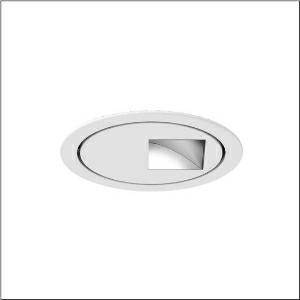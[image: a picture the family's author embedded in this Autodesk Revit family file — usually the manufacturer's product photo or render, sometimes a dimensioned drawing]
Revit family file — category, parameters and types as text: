
# Revit family: lunis_11_mini_round_51dk11b72wn21
name_source: partatom
category: Lighting Fixtures
units: mm (PartAtom-declared; Revit-internal decimal feet)

## family parameters
Cut with Voids When Loaded = No
Host = Face
Light Source = No
Part Type = Normal
Room Calculation Point = No
Round Connector Dimension = Use Diameter
Shared = No

## types (1)
- Lunis 11 mini round (1 x LED 4000K / CRI = 90 (unbekannt), 2120 lm, 4000K)
    Apparent Load = 28 VA
    CIE Flux Codes = 44 77 97 100 100
    Color Rendering = 90
    Color Temperature = 4000K
    Default Elevation = 1800 mm
    Description = Lunis 11 mini round, downlight, light control with wallwasher, of highly reflective aluminium, highly specular, light emission: direct distribution, LED rated luminous flux: 2.120lm, light colour: 940, control gear: ECG, with terminal, 3-pole, mains connection: 220..230V, AC/DC, 0/50..60Hz, LED module, luminaire module, of aluminium, highly specular, white, diameter: 176mm, clamping range: 1..40mm, recessing ring, of plastic, traffic white (RAL 9016), protection rating (complete): IP20, insulation class (complete): insulation class II (safety insulation), certification: CE, permissible ambient temperature for indoor applications: 0..+35°C, packaging unit: 1 piece
    Height = 0 mm  [stored 0 ft]
    Lamp = 1 x LED 4000K / CRI >= 90 (unbekannt)
    Lamp Light Flux = 2120 lm
    Lamp count = 1
    Length = 176 mm
    Luminous efficacy = 75 lm/W
    Manufacturer = Siteco
    ModVariant = No
    Model = 51DK11B72WN21
    Mounting Place = Ceiling
    Mounting Type = Recessed
    Number of Poles = 1
    OnlyDefault = Yes
    Power Factor = 1
    Product Name = Lunis 11 mini round
    Product group = downlight
    ProductGroupID = 400
    Protection Class = Protection class II
    Protection Degree = IP 20
    RLX_Detail_Level = 1
    RLX_Emergency_Light_Flux = 0 lm
    RLX_Emergency_Type = 0
    RLX_Emergency_Type_DB = No
    RlxData = <blob elided: 59265 chars, md5=d7e8e7a5>
    Socket = socket
    Standby Power = 0 W
    System Light Flux = 2120 lm
    System Power = 28 W
    Type Comments = Product without accessories
    Type Image = l_1004772.jpg
    URL = http://relux.com
    VarID = ---
    Voltage = 0 V
    Weight = 0.00 kg
    Width = 176 mm

note: [stored X ft] marks values corroborated as IEEE doubles in the binary element streams (Revit-internal decimal feet)

## geometry (parser evidence)
native form markers: Blend x4, Sweep x10
no freeform markers — native parametric forms only
